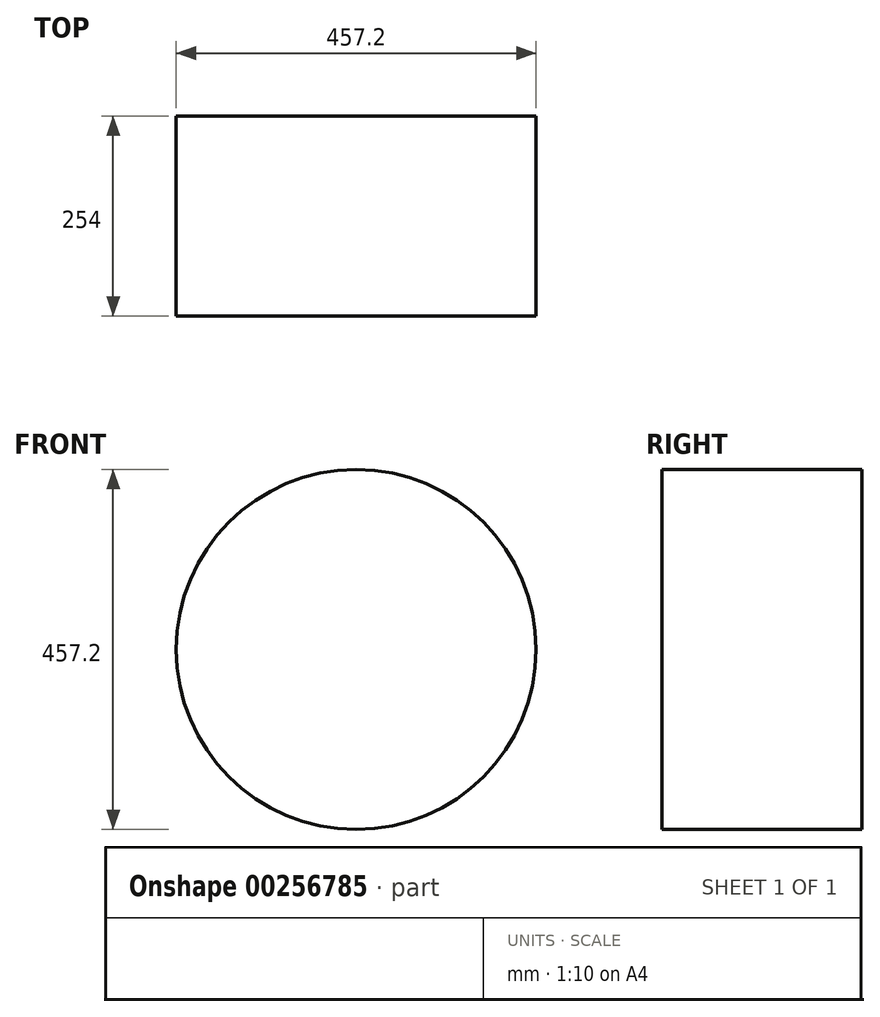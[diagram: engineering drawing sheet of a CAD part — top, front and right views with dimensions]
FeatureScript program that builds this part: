
annotation { "Feature Type Name" : "Feature", "Feature Type Description" : "" }
export const myFeature = defineFeature(function(context is Context, id is Id, definition is map)
    precondition{}
    {
        {
            var Q0;
            Q0=qCreatedBy(makeId("Front.planeOp"),FACE);
            var sketch = newSketch(context, id + "F0", { "sketchPlane" : qUnion([Q0])});
            skCircle(sketch, "E0", {"center": v(0, 0) * mm, "radius": 228.6 * mm});
            skSolve(sketch);
        }
        {
            var Q0;
            Q0 = qSketchRegion(id + "F0", true);
            extrude(context, id + "F1", {"entities" : qUnion([Q0]), "endBound" : BoundingType.SYMMETRIC, "depth" : 254 * mm});
        }
    });
